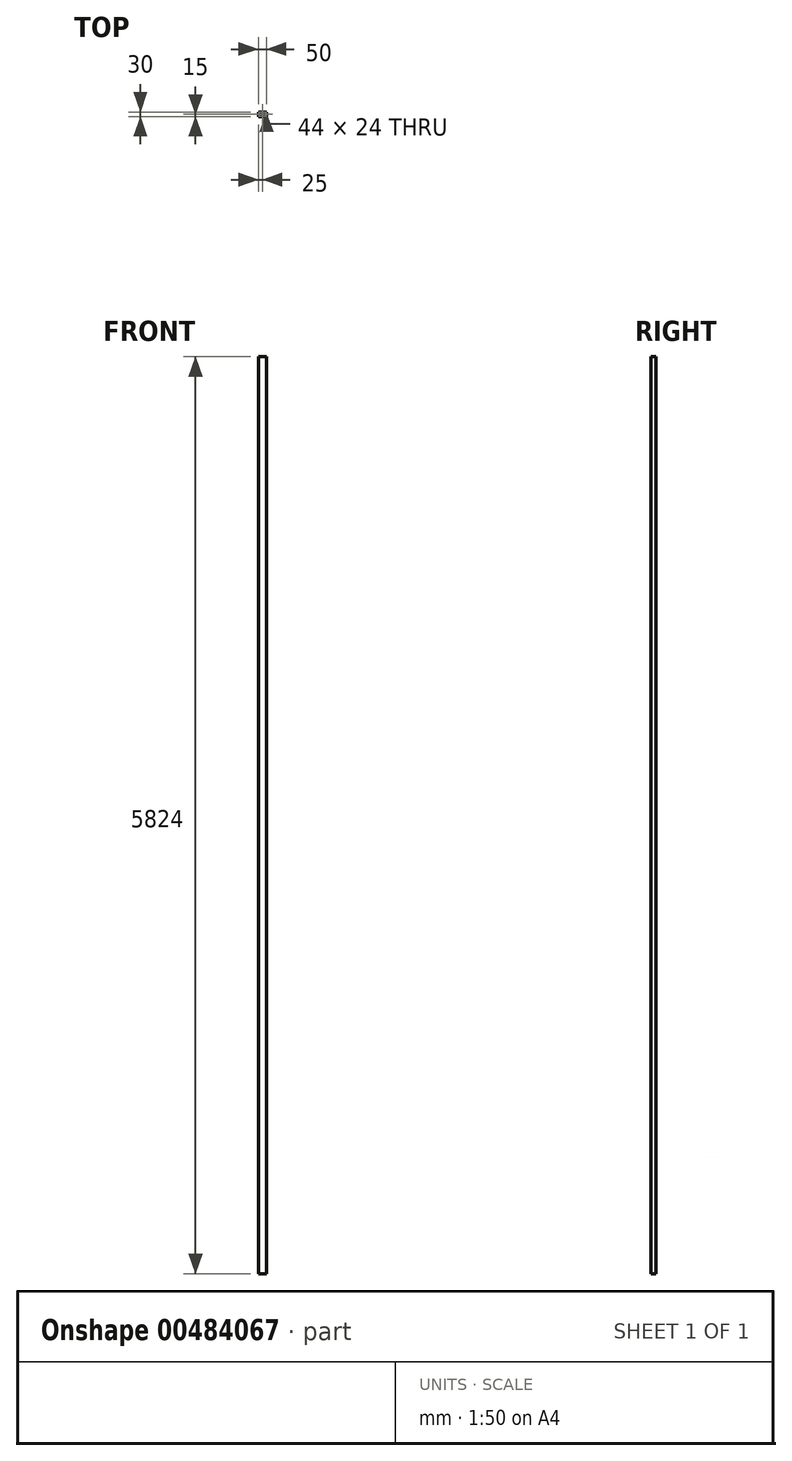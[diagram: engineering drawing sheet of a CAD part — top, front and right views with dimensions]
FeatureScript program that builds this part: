
annotation { "Feature Type Name" : "Feature", "Feature Type Description" : "" }
export const myFeature = defineFeature(function(context is Context, id is Id, definition is map)
    precondition{}
    {
        {
            var Q0;
            Q0=qCreatedBy(makeId("Top.planeOp"),FACE);
            var sketch = newSketch(context, id + "F0", { "sketchPlane" : qUnion([Q0])});
            skLineSegment(sketch, "E0.bottom", {"start": v(-50, 30) * mm, "end": v(0, 30) * mm});
            skLineSegment(sketch, "E0.top", {"start": v(-50, 0) * mm, "end": v(0, 0) * mm});
            skLineSegment(sketch, "E0.left", {"start": v(-50, 30) * mm, "end": v(-50, 0) * mm});
            skLineSegment(sketch, "E0.right", {"start": v(0, 30) * mm, "end": v(0, 0) * mm});
            skLineSegment(sketch, "E1.bottom", {"start": v(-47, 27) * mm, "end": v(-3, 27) * mm});
            skLineSegment(sketch, "E1.top", {"start": v(-47, 3) * mm, "end": v(-3, 3) * mm});
            skLineSegment(sketch, "E1.left", {"start": v(-47, 27) * mm, "end": v(-47, 3) * mm});
            skLineSegment(sketch, "E1.right", {"start": v(-3, 27) * mm, "end": v(-3, 3) * mm});
            skSolve(sketch);
        }
        {
            var Q0;
            Q0 = qSketchRegion(id + "F0", true);
            extrude(context, id + "F1", {"entities" : qUnion([Q0]), "depth" : 5824 * mm, "offsetDistance" : 25 * mm});
        }
    });
